# Revit family: Haworth_Haworth_Soji_Chair_Task_NA
name_source: partatom
category: Furniture
units: mm (PartAtom-declared; Revit-internal decimal feet)

## family parameters
Always vertical = Yes
Cut with Voids When Loaded = No
OmniClass Number = 23.40.70.14.64.11
OmniClass Title = Office Furniture
Room Calculation Point = No
Shared = No
Work Plane-Based = No

## types (6) — shared parameters
Actual Depth = 27 "
Actual Width = 28 "
Assembly Code = E2020200
Caster Finish = Haworth _ Polymer _ Black
Hardware Finish = Haworth _ Paint _ Black
High Base = Yes
Low Base = No
Lumbar Finish = Haworth _ Polymer _ Undecided
Manufacturer = Haworth
Model = Haworth Soji Chair Task
Product URL = https://www.haworth.com
Revision Number = 2
Support Finish = Haworth _ Metal _ Stainless Steel
URL = http://www.haworth.com
Warranty = http://www.haworth.com

## per-type parameters (varying)
| type | Arms | Description | Fixed Arms | Height Adjustable Arms | With Lumbar | Without Arms | Without Lumbar |
| Height Adjustable Arms - With Lumbar | Yes | Haworth Soji Chair Task - Height Adjustable Arms - With Lumbar | No | Yes | Yes | No | No |
| Height Adjustable Arms - Without Lumbar | Yes | Haworth Soji Chair Task - Height Adjustable Arms - Without Lumbar | No | Yes | No | No | Yes |
| Fixed Arms - Without Lumbar | Yes | Haworth Soji Chair Task - Fixed Arms - Without Lumbar | Yes | No | No | No | Yes |
| Fixed Arms - With Lumbar | Yes | Haworth Soji Chair Task - Fixed Arms - With Lumbar | Yes | No | Yes | No | No |
| Without Arms - Without Lumbar | No | Haworth Soji Chair Task - Without Arms - Without Lumbar | No | No | No | Yes | Yes |
| Without Arms - With Lumbar | No | Haworth Soji Chair Task - Without Arms - Without Lumbar | No | No | Yes | Yes | No |

## geometry (parser evidence)
native form markers: Sweep x14
no freeform markers — native parametric forms only
